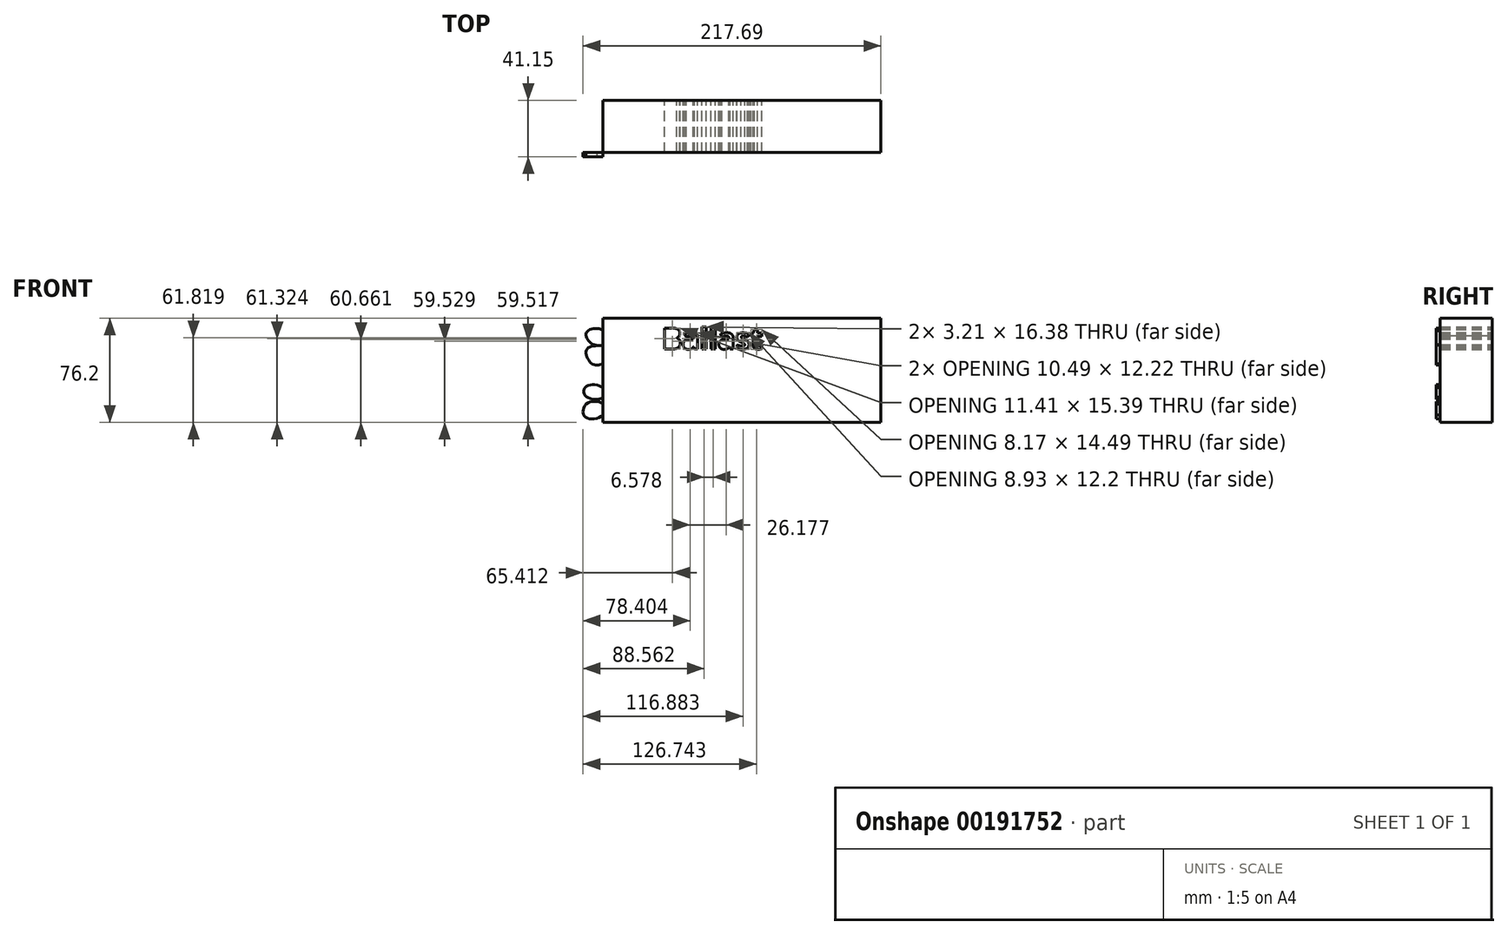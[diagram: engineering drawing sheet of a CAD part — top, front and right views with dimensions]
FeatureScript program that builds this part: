
annotation { "Feature Type Name" : "Feature", "Feature Type Description" : "" }
export const myFeature = defineFeature(function(context is Context, id is Id, definition is map)
    precondition{}
    {
        {
            var Q0;
            Q0=qCreatedBy(makeId("Front.planeOp"),FACE);
            var sketch = newSketch(context, id + "F0", { "sketchPlane" : qUnion([Q0])});
            skLineSegment(sketch, "E0.bottom", {"start": v(-72.94, 62.81) * mm, "end": v(130.26, 62.81) * mm});
            skLineSegment(sketch, "E0.top", {"start": v(-72.94, -13.39) * mm, "end": v(130.26, -13.39) * mm});
            skLineSegment(sketch, "E0.left", {"start": v(-72.94, 62.81) * mm, "end": v(-72.94, -13.39) * mm});
            skLineSegment(sketch, "E0.right", {"start": v(130.26, 62.81) * mm, "end": v(130.26, -13.39) * mm});
            skText(sketch, "E1", { "text": "Ballast", "fontName": "OpenSans-Bold.ttf"});
            const initialGuessF0  = {"E1": [-0.02966, 0.04024, 1, 0, 0.01552]};
            skSetInitialGuess(sketch, initialGuessF0);
            skSolve(sketch);
        }
        {
            var Q0;
            Q0 = qSketchRegion(id + "F0", true);
            extrude(context, id + "F1", {"entities" : qUnion([Q0]), "depth" : 38.1 * mm});
        }
        {
            var Q0;
            Q0=makeQuery(id+"F1.opExtrude","CAP_FACE",FACE,{"disambiguationData":[OSD([sQuery(id+"F0.wireOp",EDGE,"E0.bottom"),sQuery(id+"F0.wireOp",EDGE,"E0.top"),sQuery(id+"F0.wireOp",EDGE,"E0.left"),sQuery(id+"F0.wireOp",EDGE,"E0.right"),sQuery(id+"F0.wireOp",EDGE,"E1.sketch_text.stroke-0"),sQuery(id+"F0.wireOp",EDGE,"E1.sketch_text.stroke-1"),sQuery(id+"F0.wireOp",EDGE,"E1.sketch_text.stroke-2"),sQuery(id+"F0.wireOp",EDGE,"E1.sketch_text.stroke-3"),sQuery(id+"F0.wireOp",EDGE,"E1.sketch_text.stroke-4"),sQuery(id+"F0.wireOp",EDGE,"E1.sketch_text.stroke-5"),sQuery(id+"F0.wireOp",EDGE,"E1.sketch_text.stroke-6"),sQuery(id+"F0.wireOp",EDGE,"E1.sketch_text.stroke-7"),sQuery(id+"F0.wireOp",EDGE,"E1.sketch_text.stroke-8"),sQuery(id+"F0.wireOp",EDGE,"E1.sketch_text.stroke-9"),sQuery(id+"F0.wireOp",EDGE,"E1.sketch_text.stroke-10"),sQuery(id+"F0.wireOp",EDGE,"E1.sketch_text.stroke-11"),sQuery(id+"F0.wireOp",EDGE,"E1.sketch_text.stroke-25"),sQuery(id+"F0.wireOp",EDGE,"E1.sketch_text.stroke-26"),sQuery(id+"F0.wireOp",EDGE,"E1.sketch_text.stroke-27"),sQuery(id+"F0.wireOp",EDGE,"E1.sketch_text.stroke-28"),sQuery(id+"F0.wireOp",EDGE,"E1.sketch_text.stroke-29"),sQuery(id+"F0.wireOp",EDGE,"E1.sketch_text.stroke-30"),sQuery(id+"F0.wireOp",EDGE,"E1.sketch_text.stroke-31"),sQuery(id+"F0.wireOp",EDGE,"E1.sketch_text.stroke-32"),sQuery(id+"F0.wireOp",EDGE,"E1.sketch_text.stroke-33"),sQuery(id+"F0.wireOp",EDGE,"E1.sketch_text.stroke-34"),sQuery(id+"F0.wireOp",EDGE,"E1.sketch_text.stroke-35"),sQuery(id+"F0.wireOp",EDGE,"E1.sketch_text.stroke-36"),sQuery(id+"F0.wireOp",EDGE,"E1.sketch_text.stroke-37"),sQuery(id+"F0.wireOp",EDGE,"E1.sketch_text.stroke-38"),sQuery(id+"F0.wireOp",EDGE,"E1.sketch_text.stroke-39"),sQuery(id+"F0.wireOp",EDGE,"E1.sketch_text.stroke-40"),sQuery(id+"F0.wireOp",EDGE,"E1.sketch_text.stroke-41"),sQuery(id+"F0.wireOp",EDGE,"E1.sketch_text.stroke-42"),sQuery(id+"F0.wireOp",EDGE,"E1.sketch_text.stroke-50"),sQuery(id+"F0.wireOp",EDGE,"E1.sketch_text.stroke-51"),sQuery(id+"F0.wireOp",EDGE,"E1.sketch_text.stroke-52"),sQuery(id+"F0.wireOp",EDGE,"E1.sketch_text.stroke-53"),sQuery(id+"F0.wireOp",EDGE,"E1.sketch_text.stroke-54"),sQuery(id+"F0.wireOp",EDGE,"E1.sketch_text.stroke-55"),sQuery(id+"F0.wireOp",EDGE,"E1.sketch_text.stroke-56"),sQuery(id+"F0.wireOp",EDGE,"E1.sketch_text.stroke-57"),sQuery(id+"F0.wireOp",EDGE,"E1.sketch_text.stroke-58"),sQuery(id+"F0.wireOp",EDGE,"E1.sketch_text.stroke-59"),sQuery(id+"F0.wireOp",EDGE,"E1.sketch_text.stroke-60"),sQuery(id+"F0.wireOp",EDGE,"E1.sketch_text.stroke-61"),sQuery(id+"F0.wireOp",EDGE,"E1.sketch_text.stroke-62"),sQuery(id+"F0.wireOp",EDGE,"E1.sketch_text.stroke-63"),sQuery(id+"F0.wireOp",EDGE,"E1.sketch_text.stroke-64"),sQuery(id+"F0.wireOp",EDGE,"E1.sketch_text.stroke-65"),sQuery(id+"F0.wireOp",EDGE,"E1.sketch_text.stroke-66"),sQuery(id+"F0.wireOp",EDGE,"E1.sketch_text.stroke-67"),sQuery(id+"F0.wireOp",EDGE,"E1.sketch_text.stroke-68"),sQuery(id+"F0.wireOp",EDGE,"E1.sketch_text.stroke-69"),sQuery(id+"F0.wireOp",EDGE,"E1.sketch_text.stroke-70"),sQuery(id+"F0.wireOp",EDGE,"E1.sketch_text.stroke-71"),sQuery(id+"F0.wireOp",EDGE,"E1.sketch_text.stroke-72"),sQuery(id+"F0.wireOp",EDGE,"E1.sketch_text.stroke-73"),sQuery(id+"F0.wireOp",EDGE,"E1.sketch_text.stroke-74"),sQuery(id+"F0.wireOp",EDGE,"E1.sketch_text.stroke-75"),sQuery(id+"F0.wireOp",EDGE,"E1.sketch_text.stroke-83"),sQuery(id+"F0.wireOp",EDGE,"E1.sketch_text.stroke-84"),sQuery(id+"F0.wireOp",EDGE,"E1.sketch_text.stroke-85"),sQuery(id+"F0.wireOp",EDGE,"E1.sketch_text.stroke-86"),sQuery(id+"F0.wireOp",EDGE,"E1.sketch_text.stroke-87"),sQuery(id+"F0.wireOp",EDGE,"E1.sketch_text.stroke-88"),sQuery(id+"F0.wireOp",EDGE,"E1.sketch_text.stroke-89"),sQuery(id+"F0.wireOp",EDGE,"E1.sketch_text.stroke-90"),sQuery(id+"F0.wireOp",EDGE,"E1.sketch_text.stroke-91"),sQuery(id+"F0.wireOp",EDGE,"E1.sketch_text.stroke-92"),sQuery(id+"F0.wireOp",EDGE,"E1.sketch_text.stroke-93"),sQuery(id+"F0.wireOp",EDGE,"E1.sketch_text.stroke-94"),sQuery(id+"F0.wireOp",EDGE,"E1.sketch_text.stroke-95"),sQuery(id+"F0.wireOp",EDGE,"E1.sketch_text.stroke-96"),sQuery(id+"F0.wireOp",EDGE,"E1.sketch_text.stroke-97"),sQuery(id+"F0.wireOp",EDGE,"E1.sketch_text.stroke-98"),sQuery(id+"F0.wireOp",EDGE,"E1.sketch_text.stroke-99"),sQuery(id+"F0.wireOp",EDGE,"E1.sketch_text.stroke-100"),sQuery(id+"F0.wireOp",EDGE,"E1.sketch_text.stroke-101"),sQuery(id+"F0.wireOp",EDGE,"E1.sketch_text.stroke-102"),sQuery(id+"F0.wireOp",EDGE,"E1.sketch_text.stroke-103"),sQuery(id+"F0.wireOp",EDGE,"E1.sketch_text.stroke-104"),sQuery(id+"F0.wireOp",EDGE,"E1.sketch_text.stroke-105"),sQuery(id+"F0.wireOp",EDGE,"E1.sketch_text.stroke-106"),sQuery(id+"F0.wireOp",EDGE,"E1.sketch_text.stroke-107"),sQuery(id+"F0.wireOp",EDGE,"E1.sketch_text.stroke-108"),sQuery(id+"F0.wireOp",EDGE,"E1.sketch_text.stroke-109"),sQuery(id+"F0.wireOp",EDGE,"E1.sketch_text.stroke-110"),sQuery(id+"F0.wireOp",EDGE,"E1.sketch_text.stroke-111"),sQuery(id+"F0.wireOp",EDGE,"E1.sketch_text.stroke-112"),sQuery(id+"F0.wireOp",EDGE,"E1.sketch_text.stroke-113"),sQuery(id+"F0.wireOp",EDGE,"E1.sketch_text.stroke-114"),sQuery(id+"F0.wireOp",EDGE,"E1.sketch_text.stroke-115"),sQuery(id+"F0.wireOp",EDGE,"E1.sketch_text.stroke-116"),sQuery(id+"F0.wireOp",EDGE,"E1.sketch_text.stroke-117"),sQuery(id+"F0.wireOp",EDGE,"E1.sketch_text.stroke-118"),sQuery(id+"F0.wireOp",EDGE,"E1.sketch_text.stroke-119"),sQuery(id+"F0.wireOp",EDGE,"E1.sketch_text.stroke-120"),sQuery(id+"F0.wireOp",EDGE,"E1.sketch_text.stroke-121"),sQuery(id+"F0.wireOp",EDGE,"E1.sketch_text.stroke-122"),sQuery(id+"F0.wireOp",EDGE,"E1.sketch_text.stroke-123"),sQuery(id+"F0.wireOp",EDGE,"E1.sketch_text.stroke-124"),sQuery(id+"F0.wireOp",EDGE,"E1.sketch_text.stroke-125"),sQuery(id+"F0.wireOp",EDGE,"E1.sketch_text.stroke-126")])],"isStart":false});
            var sketch = newSketch(context, id + "F2", { "sketchPlane" : qUnion([Q0])});
            skFitSpline(sketch, "E2", {"points": [v(-72.94, 53.5) * mm, v(-84.64, 52.71) * mm, v(-80.37, 43.78) * mm, v(-72.94, 43) * mm, v(-72.94, 43.39) * mm, v(-72.94, 53.5) * mm]});
            skFitSpline(sketch, "E3", {"points": [v(-72.94, 43) * mm, v(-85.03, 39.5) * mm, v(-80.75, 29.4) * mm, v(-72.94, 29.4) * mm], "startDerivative": vector(-44.38, -1.8) * mm, "endDerivative": vector(27.88, 8.4) * mm});
            skFitSpline(sketch, "E4", {"points": [v(-72.94, 43.39) * mm, v(-72.94, 29.4) * mm], "startDerivative": vector(0, -14) * mm, "endDerivative": vector(0, -14) * mm});
            skFitSpline(sketch, "E5", {"points": [v(-72.94, 11.9) * mm, v(-85.42, 12.68) * mm, v(-85.42, 5.69) * mm, v(-72.94, 4.91) * mm, v(-72.94, 11.9) * mm]});
            skFitSpline(sketch, "E6", {"points": [v(-72.94, 0) * mm, v(-85.03, 0) * mm, v(-85.8, -9.47) * mm, v(-72.94, -7.91) * mm, v(-72.94, 0) * mm]});
            skSolve(sketch);
        }
        {
            var Q0;
            {var subQ1=sQuery(id+"F2.wireOp",EDGE,"E3");var subQ2=sQuery(id+"F2.wireOp",EDGE,"E2");var subQ6=makeQuery(id+"F2.imprint","INTERSECT",VERTEX,{"derivedFrom":[subQ2,subQ1]});Q0=makeQuery(id+"F2.imprint","IMPRINT",FACE,{"disambiguationData":[TD([[makeQuery(id+"F2.imprint","IMPRINT",EDGE,{"disambiguationData":[TD([[subQ6,1.0]])],"derivedFrom":subQ2}),1.0]])]});}
            var Q1;
            {var subQ1=sQuery(id+"F2.wireOp",EDGE,"E3");var subQ2=sQuery(id+"F2.wireOp",EDGE,"E2");var subQ4=makeQuery(id+"F2.imprint","INTERSECT",VERTEX,{"derivedFrom":[subQ2,subQ1]});Q1=makeQuery(id+"F2.imprint","IMPRINT",FACE,{"disambiguationData":[TD([[makeQuery(id+"F2.imprint","IMPRINT",EDGE,{"disambiguationData":[TD([[subQ4,-1.0]])],"derivedFrom":subQ2}),-1.0]])]});}
            var Q2;
            {var subQ0=sQuery(id+"F2.wireOp",EDGE,"E5");var subQ1=makeQuery(id+"F1.opExtrude","CAP_EDGE",EDGE,{"disambiguationData":[OSD([sQuery(id+"F0.wireOp",EDGE,"E0.left")])],"isStart":false});var subQ2=makeQuery(id+"F2.imprint","INTERSECT",VERTEX,{"disambiguationData":[OD(0.0)],"derivedFrom":[subQ1,subQ0]});Q2=makeQuery(id+"F2.imprint","IMPRINT",FACE,{"disambiguationData":[TD([[makeQuery(id+"F2.imprint","IMPRINT",EDGE,{"disambiguationData":[TD([[subQ2,-1.0]])],"derivedFrom":subQ0}),1.0]])]});}
            var Q3;
            {var subQ0=sQuery(id+"F2.wireOp",EDGE,"E6");var subQ1=makeQuery(id+"F1.opExtrude","CAP_EDGE",EDGE,{"disambiguationData":[OSD([sQuery(id+"F0.wireOp",EDGE,"E0.left")])],"isStart":false});var subQ2=makeQuery(id+"F2.imprint","INTERSECT",VERTEX,{"disambiguationData":[OD(0.0)],"derivedFrom":[subQ1,subQ0]});Q3=makeQuery(id+"F2.imprint","IMPRINT",FACE,{"disambiguationData":[TD([[makeQuery(id+"F2.imprint","IMPRINT",EDGE,{"disambiguationData":[TD([[subQ2,1.0]])],"derivedFrom":subQ0}),1.0]])]});}
            extrude(context, id + "F3", {"entities" : qUnion([Q0, Q1, Q2, Q3]), "depth" : 3.05 * mm});
        }
    });
